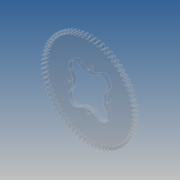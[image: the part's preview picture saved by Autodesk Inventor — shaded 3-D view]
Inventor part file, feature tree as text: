
AUTODESK INVENTOR PART (.ipt)
format: ipt  version: 2017 (Build 210142000, 142)  size: 437,248 bytes
history: native  units: mm
features: other x6, reference x5, extrude x1, sketch x1
ambient origin geometry x8: Origin, YZ Plane, XZ Plane, XY Plane, X Axis, Y Axis, Z Axis, Center Point
bodies: Body1 (feature_tree)
feature tree (13):
  other  "Sólido1"
  extrude  "Extrusión1"  Depth=5.0mm
  other  "Dientes de engranaje recto1"
  sketch  "Boceto1"  dims[d0=30.0mm d1=150.0mm d2=5.0mm d3=0.0mm]
  reference  "Referencia1"
  reference  "Referencia2"
  reference  "Referencia3"
  reference  "Referencia4"
  reference  "Referencia5"
  other  "Engranaje recto2"
  other  "<userpath>\Dropbox\E\Caja Motriz\transmision Engranajes\Plato Carrete.iam"
  other  "Plato Carrete.iam"
  other  "carrete:1"
